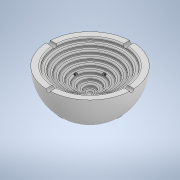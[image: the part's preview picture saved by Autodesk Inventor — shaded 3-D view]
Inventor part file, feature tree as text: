
AUTODESK INVENTOR PART (.ipt)
format: ipt  version: 2022 (Build 260153000, 153)  size: 514,560 bytes
history: native  units: mm
features: extrude x16, sketch x16, other x9, fillet x5
ambient origin geometry x8: Origin, YZ Plane, XZ Plane, XY Plane, X Axis, Y Axis, Z Axis, Center Point
bodies: Body1 (feature_tree)
feature tree (46):
  other  "實體1"
  extrude  "擠出1"  Depth=60.0mm
  fillet  "圓角1"  Radius=30.0mm
  extrude  "擠出2"  Depth=30.0mm
  extrude  "擠出3"  Depth=50.0mm
  extrude  "擠出4"  Depth=2.0mm TaperAngle=0.0deg
  extrude  "擠出5"  Depth=44.0mm
  extrude  "擠出6"  Depth=2.0mm TaperAngle=0.0deg
  extrude  "擠出7"  Depth=38.0mm
  extrude  "擠出8"  Depth=2.0mm TaperAngle=0.0deg
  extrude  "擠出9"  Depth=32.0mm
  extrude  "擠出11"  Depth=2.0mm TaperAngle=0.0deg
  extrude  "擠出12"  Depth=26.0mm
  extrude  "擠出13"  Depth=2.0mm TaperAngle=0.0deg
  extrude  "擠出16"  Depth=20.0mm
  fillet  "圓角2"  Radius=2.0mm
  extrude  "擠出17"  Depth=14.0mm
  fillet  "圓角3"  Radius=2.0mm
  extrude  "擠出18"  Depth=8.0mm
  fillet  "圓角4"  Radius=2.0mm
  extrude  "擠出19"  Depth=3.0mm
  fillet  "圓角5"  Radius=20.0mm
  other  "面圓角1"
  other  "面圓角2"
  other  "面圓角3"
  other  "面圓角4"
  other  "面圓角5"
  other  "面圓角6"
  other  "面圓角7"
  other  "面圓角8"
  sketch  "草圖3"
  sketch  "草圖4"
  sketch  "草圖5"
  sketch  "草圖6"
  sketch  "草圖7"
  sketch  "草圖8"
  sketch  "草圖9"
  sketch  "草圖10"
  sketch  "草圖11"
  sketch  "草圖14"
  sketch  "草圖15"
  sketch  "草圖16"
  sketch  "草圖25"
  sketch  "草圖26"
  sketch  "草圖27"
  sketch  "草圖29"
